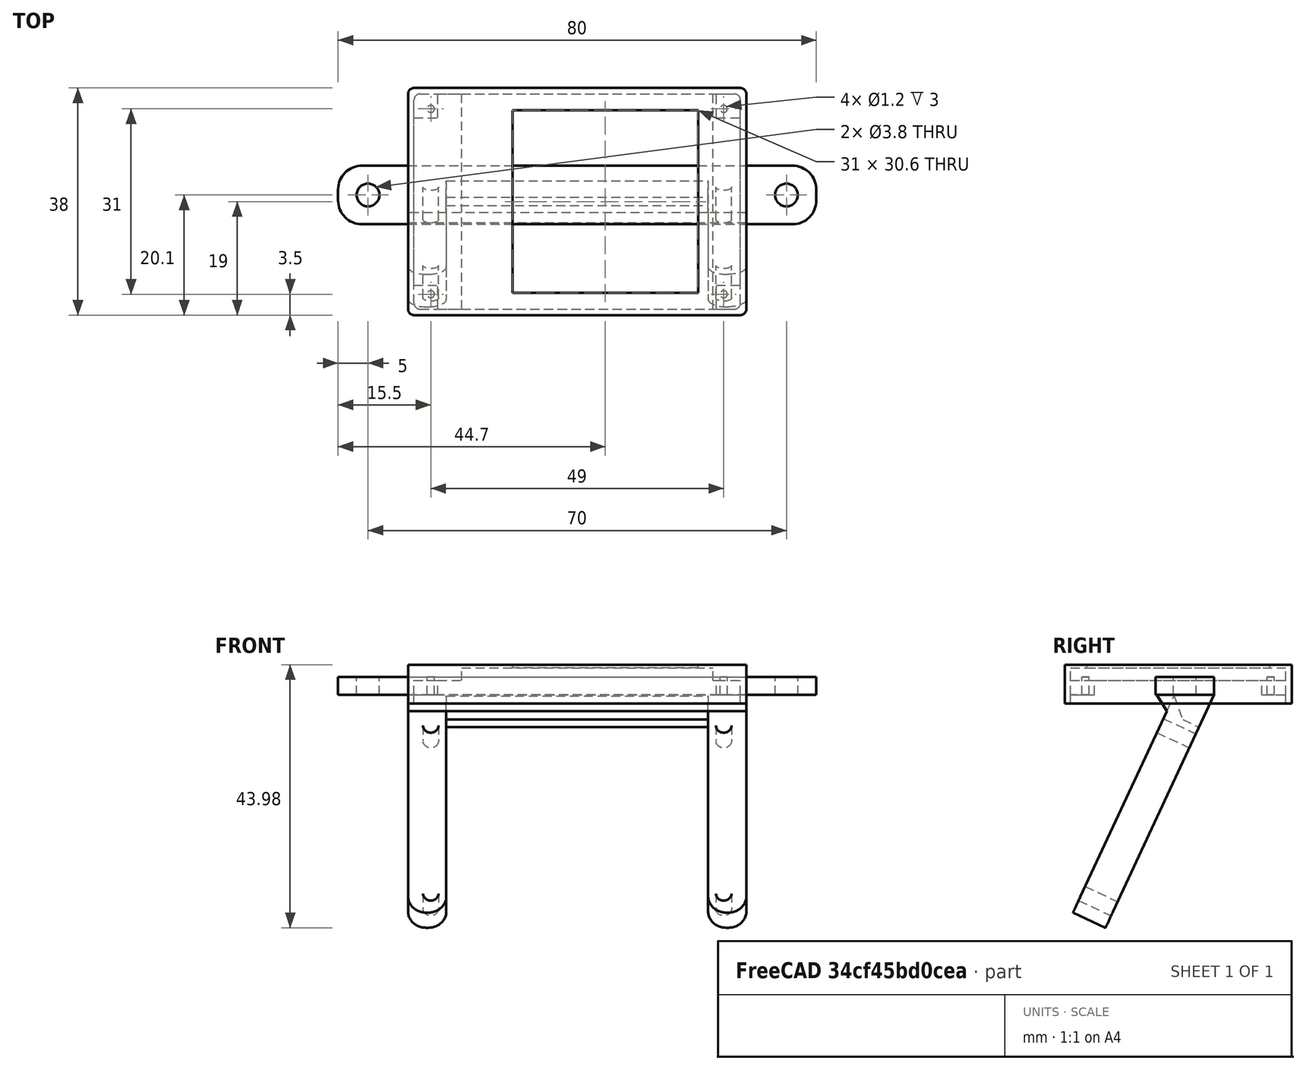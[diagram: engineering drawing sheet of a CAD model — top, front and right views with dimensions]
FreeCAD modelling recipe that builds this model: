
FCSTD DOCUMENT  (FreeCAD 0.19R)
Label: lcd1.6
License: FreeArt
LicenseURL: http://artlibre.org/licence/lal
objects: Part::Box×8, Part::FeaturePython×4, Part::Fillet×4, Part::Cut×4, Part::MultiFuse×4, Part::Cylinder×3, Spreadsheet::Sheet×1, Part::Chamfer×1
note: 28 computed .brp shape members not serialized (recipe doc carries the construction recipe); baked Part::Feature solids carry a one-line shape summary decoded from their .brp

FEATURE [Part::Box] Box  label="top cover cube"
  AttacherType = Attacher::AttachEngine3D
  Height = 6.5
  Length = 56.6
  Placement = pos=(0,0,-1.5) rot=(0,0,1;0rad)
  Width = 38
  expr: Length = 2 * <<p>>.side_wall + <<p>>.pcb_x
  expr: Width = 2 * <<p>>.side_wall + <<p>>.pcb_y
  expr: Height = <<p>>.lcd_h + <<p>>.pcb_h + 1
  expr: .Placement.Base.z = -<<p>>.pcb_h
FEATURE [Spreadsheet::Sheet] Spreadsheet  label="p"
  cells = A1=pcb_x; B1(pcb_x)=54.6; A2=pcb_y; B2(pcb_y)=36; A3=pcb_h; B3(pcb_h)=1.5; A4=lcd_x; B4(lcd_x)=42; A5=lcd_y; B5(lcd_y)=36; A6=lcd_x_off; B6(lcd_x_off)=8; A7=lcd_h; B7(lcd_h)=4; A8=display_x; B8(display_x)=31; A9=display_y; B9(display_y)=30.6; A10=display_x_off; B10(display_x_off)=8.5; A11=display_y_off; B11(display_y_off)==(lcd_y - display_y) / 2; A12=hole_r; B12(hole_r)=0.6; A13=hole_dist_x; B13(hole_dist_x)=49; A14=hole_dist_y; B14(hole_dist_y)=31; A15=pcb_above; B15(pcb_above)=2.4; A16=pcb_under; B16(pcb_under)=2; A17=pins_x; B17(pins_x)=3.4; A18=pins_y; B18(pins_y)=21; A19=pins_x_off; B19(pins_x_off)=5.4; A20=pins_y_off; B20(pins_y_off)=0; A21=attach_hole_dist; B21(attach_hole_dist)=10; A22=attach_hole_r; B22(attach_hole_r)=1.9; A23=attach_hole_wall; B23(attach_hole_wall)=3; A24=attach_z; B24(attach_z)=3; A25=hole_stand_x; B25(hole_stand_x)=4; A26=hole_stand_y; B26(hole_stand_y)=4; A27=side_wall; B27(side_wall)=1; A28=wall; B28(wall)=2; A29=back_wall; B29(back_wall)=6; A30=bolt_hole_r; B30(bolt_hole_r)=1.3; A31=back_bottom_extra; B31(back_bottom_extra)=5
FEATURE [Part::Box] Box001  label="lcd extract"
  AttacherType = Attacher::AttachEngine3D
  Height = 4.5
  Length = 42
  Placement = pos=(9,1,0) rot=(0,0,1;0rad)
  Width = 36
  expr: Length = <<p>>.lcd_x
  expr: Width = <<p>>.lcd_y
  expr: .Placement.Base.x = <<p>>.side_wall + <<p>>.lcd_x_off
  expr: .Placement.Base.y = <<p>>.side_wall
  expr: Height = <<p>>.lcd_h + 0.5
FEATURE [Part::Box] Box002  label="hole stand"
  AttacherType = Attacher::AttachEngine3D
  Height = 2.4
  Length = 4
  Placement = pos=(1,1,0) rot=(0,0,1;0rad)
  Width = 4
  expr: Length = <<p>>.hole_stand_x
  expr: Width = <<p>>.hole_stand_y
  expr: Height = <<p>>.pcb_above
  expr: .Placement.Base.x = <<p>>.side_wall
  expr: .Placement.Base.y = <<p>>.side_wall
FEATURE [Part::FeaturePython] Array  label="hole stand array"  # Draft array (typed FeaturePython)
  Angle = 360
  ArrayType = 0
  Axis = (0,0,1)
  Base = -> Box002
  Center = (0,0,0)
  Fuse = false
  IntervalAxis = (0,0,0)
  IntervalX = (50.6,0,0)
  IntervalY = (0,32,0)
  IntervalZ = (0,0,1)
  NumberPolar = 1
  NumberX = 2
  NumberY = 2
  NumberZ = 1
  expr: .IntervalY.y = <<p>>.pcb_y - <<p>>.hole_stand_y
  expr: .IntervalX.x = <<p>>.pcb_x - <<p>>.hole_stand_x
FEATURE [Part::Box] Box003  label="top cover extract cube"
  AttacherType = Attacher::AttachEngine3D
  Height = 3.9
  Length = 54.6
  Placement = pos=(1,1,-1.5) rot=(0,0,1;0rad)
  Width = 36
  expr: Length = <<p>>.pcb_x
  expr: Width = <<p>>.pcb_y
  expr: Height = <<p>>.pcb_above + <<p>>.pcb_h
  expr: .Placement.Base.z = -<<p>>.pcb_h
  expr: .Placement.Base.y = <<p>>.side_wall
  expr: .Placement.Base.x = <<p>>.side_wall
FEATURE [Part::Cylinder] Cylinder  label="hole"
  Angle = 360
  AttacherType = Attacher::AttachEngine3D
  Height = 3
  Placement = pos=(3.8,3.5,0) rot=(0,0,1;0rad)
  Radius = 0.6
  expr: Radius = <<p>>.hole_r
  expr: .Placement.Base.x = (2 * <<p>>.side_wall + <<p>>.pcb_x - <<p>>.hole_dist_x) / 2
  expr: .Placement.Base.y = (2 * <<p>>.side_wall + <<p>>.pcb_y - <<p>>.hole_dist_y) / 2
  expr: Height = <<p>>.lcd_h - 1
FEATURE [Part::FeaturePython] Array001  label="hole array"  # Draft array (typed FeaturePython)
  Angle = 360
  ArrayType = 0
  Axis = (0,0,1)
  Base = -> Cylinder
  Center = (0,0,0)
  Fuse = false
  IntervalAxis = (0,0,0)
  IntervalX = (49,0,0)
  IntervalY = (0,31,0)
  IntervalZ = (0,0,1)
  NumberPolar = 1
  NumberX = 2
  NumberY = 2
  NumberZ = 1
  expr: .IntervalX.x = <<p>>.hole_dist_x
  expr: .IntervalY.y = <<p>>.hole_dist_y
FEATURE [Part::Fillet] Fillet  label="top cover fillet"
  Base = -> Box
  Edges = 4 edges r=1: [Edge1,Edge3,Edge5,Edge7]
FEATURE [Part::Fillet] Fillet001  label="top cover extract fillet"
  Base = -> Box003
  Edges = 4 edges r=1: [Edge1,Edge3,Edge5,Edge7]
FEATURE [Part::Cut] Cut  label="top cover cut"
  Base = -> Fillet
  Tool = -> Fillet001
FEATURE [Part::MultiFuse] Fusion  label="top cover"
  Shapes = -> [Cut,Array]
FEATURE [Part::Box] Box005  label="ears cube"
  AttacherType = Attacher::AttachEngine3D
  Height = 3
  Length = 80
  Width = 9.8
  expr: Width = (<<p>>.attach_hole_r + <<p>>.attach_hole_wall) * 2
  expr: Length = floor((<<p>>.pcb_x + 2 * <<p>>.side_wall) / <<p>>.attach_hole_dist + 3) * <<p>>.attach_hole_dist
  expr: Height = <<p>>.attach_z
FEATURE [Part::Fillet] Fillet002  label="ears cube fillet"
  Base = -> Box005
  Edges = 4 edges r=4: [Edge1,Edge3,Edge5,Edge7]
FEATURE [Part::Cylinder] Cylinder001  label="attach hole"
  Angle = 360
  AttacherType = Attacher::AttachEngine3D
  Height = 10
  Placement = pos=(5,4.9,0) rot=(0,0,1;0rad)
  Radius = 1.9
  expr: Radius = <<p>>.attach_hole_r
  expr: .Placement.Base.y = <<p>>.attach_hole_r + <<p>>.attach_hole_wall
  expr: .Placement.Base.x = <<p>>.attach_hole_dist / 2
FEATURE [Part::FeaturePython] Array002  label="attach hole array"  # Draft array (typed FeaturePython)
  Angle = 360
  ArrayType = 0
  Axis = (0,0,1)
  Base = -> Cylinder001
  Center = (0,0,0)
  Fuse = false
  IntervalAxis = (0,0,0)
  IntervalX = (70,0,0)
  IntervalY = (0,1,0)
  IntervalZ = (0,0,1)
  NumberPolar = 1
  NumberX = 2
  NumberY = 1
  NumberZ = 1
  expr: .IntervalX.x = floor((<<p>>.pcb_x + 2 * <<p>>.side_wall) / <<p>>.attach_hole_dist + 2) * <<p>>.attach_hole_dist
FEATURE [Part::Cut] Cut002  label="attach plane"
  Base = -> Fillet002
  Placement = pos=(-11.7,15.2,0) rot=(0,0,1;0rad)
  Tool = -> Array002
  expr: .Placement.Base.x = -(floor(<<p>>.pcb_x / <<p>>.attach_hole_dist + 3) * <<p>>.attach_hole_dist - <<p>>.side_wall * 2 - <<p>>.pcb_x) / 2
FEATURE [Part::Box] Box006  label="lcd back holder"
  AttacherType = Attacher::AttachEngine3D
  Height = 6
  Length = 56.6
  Placement = pos=(0,-5,0) rot=(0,0,1;0rad)
  Width = 43
  expr: Length = 2 * <<p>>.side_wall + <<p>>.pcb_x
  expr: Height = <<p>>.back_wall
  expr: Width = 2 * <<p>>.side_wall + <<p>>.pcb_y + <<p>>.back_bottom_extra
  expr: .Placement.Base.y = -<<p>>.back_bottom_extra
FEATURE [Part::Box] Box007  label="lcd back holder extraction"
  AttacherType = Attacher::AttachEngine3D
  Height = 6
  Length = 43.8
  Placement = pos=(6.4,1,0) rot=(0,0,1;0rad)
  Width = 72
  expr: Length = <<p>>.pcb_x - 2 * <<p>>.pins_x_off
  expr: Height = <<p>>.back_wall
  expr: Width = <<p>>.pcb_y * 2 * <<p>>.side_wall
  expr: .Placement.Base.x = <<p>>.side_wall + <<p>>.pins_x_off
  expr: .Placement.Base.y = <<p>>.side_wall + <<p>>.pins_y_off
FEATURE [Part::Cylinder] Cylinder002  label="hole001"
  Angle = 360
  AttacherType = Attacher::AttachEngine3D
  Height = 10
  Placement = pos=(3.8,3.5,0) rot=(0,0,1;0rad)
  Radius = 1.3
  expr: Radius = <<p>>.bolt_hole_r
  expr: .Placement.Base.x = (2 * <<p>>.side_wall + <<p>>.pcb_x - <<p>>.hole_dist_x) / 2
  expr: .Placement.Base.y = (2 * <<p>>.side_wall + <<p>>.pcb_y - <<p>>.hole_dist_y) / 2
FEATURE [Part::FeaturePython] Array003  label="hole array001"  # Draft array (typed FeaturePython)
  Angle = 360
  ArrayType = 0
  Axis = (0,0,1)
  Base = -> Cylinder002
  Center = (0,0,0)
  Fuse = false
  IntervalAxis = (0,0,0)
  IntervalX = (49,0,0)
  IntervalY = (0,31,0)
  IntervalZ = (0,0,1)
  NumberPolar = 1
  NumberX = 2
  NumberY = 2
  NumberZ = 1
  expr: .IntervalX.x = <<p>>.hole_dist_x
  expr: .IntervalY.y = <<p>>.hole_dist_y
FEATURE [Part::MultiFuse] Fusion002  label="back extraction fusion"
  Shapes = -> [Array003,Box007]
FEATURE [Part::Cut] Cut003  label="back cut"
  Base = -> Box006
  Tool = -> Fusion002
FEATURE [Part::Fillet] Fillet003  label="back cut fillet"
  Base = -> Cut003
  Edges = 4 edges r=3: [Edge3,Edge19,Edge29,Edge32]
  Placement = pos=(0,17.46,-2) rot=(-1,0,0;2.00713rad)
FEATURE [Part::Box] Box008  label="display_hole"
  AttacherType = Attacher::AttachEngine3D
  Height = 10
  Length = 31
  Placement = pos=(17.5,3.7,0) rot=(0,0,1;0rad)
  Width = 30.6
  expr: Length = <<p>>.display_x
  expr: Width = <<p>>.display_y
  expr: .Placement.Base.y = <<p>>.side_wall + <<p>>.display_y_off
  expr: .Placement.Base.x = <<p>>.side_wall + <<p>>.lcd_x_off + <<p>>.display_x_off
FEATURE [Part::MultiFuse] Fusion001  label="hole fusion"
  Shapes = -> [Box001,Array001,Box008]
FEATURE [Part::Cut] Cut001  label="lcb top cover cut"
  Base = -> Fusion
  Tool = -> Fusion001
FEATURE [Part::MultiFuse] Fusion003  label="back holder fusion"
  Shapes = -> [Cut002,Fillet003]
FEATURE [Part::Chamfer] Chamfer  label="lcd back holder chamber"
  Base = -> Fusion003
  Edges = 2 edges r=3: [Edge19,Edge45]
